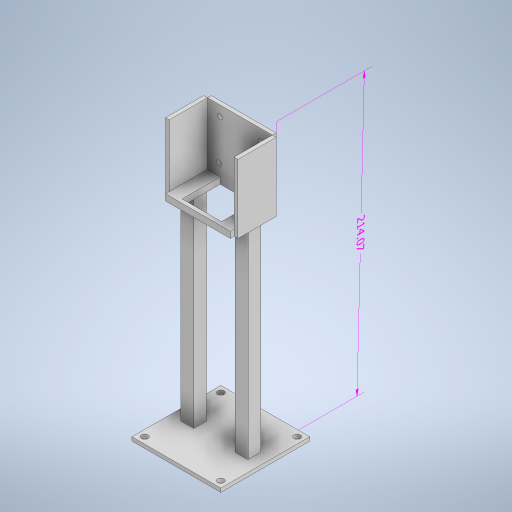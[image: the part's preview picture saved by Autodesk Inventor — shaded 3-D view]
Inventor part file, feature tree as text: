
AUTODESK INVENTOR PART (.ipt)
format: ipt  version: 2023 (Build 270158000, 158)  size: 384,000 bytes
history: native  units: mm
features: extrude x7, sketch x7, other x3
ambient origin geometry x8: Origin, YZ Plane, XZ Plane, XY Plane, X Axis, Y Axis, Z Axis, Center Point
bodies: Body1 (feature_tree)
feature tree (17):
  other  "Sólido1"
  other  "Anotaciones"
  extrude  "Extrusión1"  Depth=5.0mm TaperAngle=0.0deg
  extrude  "Extrusión4"  Depth=30.0mm
  extrude  "Extrusión5"  Depth=36.0mm
  extrude  "Extrusión6"  TaperAngle=0.0deg  [1 undecoded]
  extrude  "Extrusión7"  Depth=49.0mm
  extrude  "Extrusión8"  Depth=9.0mm
  extrude  "Extrusión9"  Depth=49.0mm TaperAngle=0.0deg
  sketch  "Boceto1"  dims[d2=10.0mm d7=5.0mm d8=0.0mm]
  sketch  "Boceto4"  dims[d21=51.0mm d22=30.0mm]
  sketch  "Boceto5"  dims[d23=57.0mm d24=36.0mm]
  sketch  "Boceto6"  dims[d25=5.0mm d26=0.0mm d27=0.0mm]
  sketch  "Boceto7"  dims[d28=49.0mm d29=0.0mm d30=4.0mm]
  sketch  "Boceto9"  dims[d31=9.0mm d32=9.0mm]
  sketch  "Boceto11"  dims[d33=40.0mm d35=360.0deg d37=49.0mm d38=0.0mm d39=49.0mm d40=0.0mm d41=10.0mm d42=10.0mm d43=20.0mm d45=360.0deg d47=160.0mm d48=0.0mm d52=70.0mm d53=70.0mm d54=70.0mm d55=70.0mm d56=60.0mm d57=5.2mm d58=5.2mm d59=5.2mm d60=5.2mm d61=3.0mm d62=0.0mm d49=5.682437mm d50=5.981921mm d51=214.070666mm]
  other  "Cota lineal 1"
note: 1 required parameter value undecoded (feature->parameter linkage not recoverable at this tier; creation-order binding heuristic only, values carry confidence <= 0.55)
